# Revit family: IS_Connect_E5042_BIM_DE
name_source: partatom
category: Plumbing Fixtures
revit_build: Autodesk Revit MEP 2016 (Build: 20161004_0715(x64)
units: mm (PartAtom-declared; Revit-internal decimal feet)

## family parameters
Cut with Voids When Loaded = Yes
Host = Face
OmniClass Number = 23.45.05.14.14
OmniClass Title = Sinks/Lavatories
Part Type = Normal
Room Calculation Point = No
Round Connector Dimension = Use Diameter
Shared = Yes

## types (2) — shared parameters
Accessories = www.idealstandard.de\ersatzteile
AreaUnits = millimeters
Assembly Code = C1030200
AssetType = Fixed
BIMobject category = Basins
BarCode = 5017830446798
Brand url = http://www.idealstandard.co.uk
CodePerformance = DIN EN 14688 CL 15, DIN EN 31
Color = White
ConnectionType = Plumbing
CurrencyUnit = €
Date of publishing = 4/3/2017
Default Elevation = 850 mm  [stored 2.78871 ft]
Description = CONNECT countertop washbasin 480x480mm, 1 taphole, with overflow
DurationUnit = year
EAN code = https://5017830446798
Edition number = 1
ExpectedLife = 25
Features = CONNECT countertop washbasin 480x480mm, 1 taphole, with overflow
Finish = White
GrossWeight = 10,59 kg
IFC Classification = Sanitary Terminal
Installation instructions = http://www.idealstandard.de
InstallationDate = 1900-12-31T23:59:59
InstallationInstructions = www.idealstandard.de\produkte
LinearUnits = millimeters
Manufacturer name = Ideal Standard
ManufacturerURL = www.idealstandard.de
Material = Vitreous china
Material main = Ceramics
ModelNumber = E504201
ModelReference = IS Einbauwaschtisch CONNECT, rund, 1Hl., m.Ül., 480x480x175mm, Weiß
NBS Reference Code = 31-79
NBS Reference Description = Sinks, Wash Basins And Troughs
Nominal height = 175 mm  [stored 0.574147 ft]
Nominal width = 480 mm  [stored 1.5748 ft]
NominalLength = 480 mm  [stored 1.5748 ft]
OmniClass Code = 23-31 13 00
OmniClass Description = Sinks
Product Guid = 4080ecf9-aefb-4d4f-9e86-ad151e22f48a
Product SKU = E5042
Product data url = https://bimobject.com
Product family = CONNECT
Product group = Basin
Product url = http://www.idealstandard.de
ProductInformation = www.idealstandard.de
QR code = http://bimobject.com
Shape = Sculptured
Size = 480 x 480 x 175 mm
Space = Internal
Technical description = http://www.idealstandard.de
URL = www.idealstandard.de
Uniclass 1.4 Code = L7212
Uniclass 1.4 Description = Washbasins
Uniclass 2.0 Code = PR-31-79
Uniclass 2.0 Description = Sinks, Wash Basins And Troughs
Uniclass 2015 Code = Pr_40_20_96
Uniclass 2015 Name = Wash basins, sinks and troughs
Uniclass2015Code = Pr_40_20_96_18
Uniclass2015Title = Counter top wash basins
Uniclass2015Version = Products v1.1
Version = 1
VolumeUnits = Litres
WasteCover = ISI_IdealStandard_BasinMaterial_White3_Render
Weight Net (Kg) = 7.94
zero-valued in all types: CWFU, Cost, HWFU, NominalDepth, WFU

## per-type parameters (varying)
| type | BIMObjectName | Model | Name |
| E504201 CONNECT countertop washbasin 480x480mm, 1 taphole, with overflow | ISI_IdealStandard_Sinks_CONNECT_E504201 | E504201 | ISI_IdealStandard_Sinks_CONNECT_E504201 |
| E5042MA CONNECT countertop washbasin 480x480mm, 1 taphole, with overflow with Ideal Plus | ISI_IdealStandard_Sinks_CONNECT_E5042MA | E5042MA | ISI_IdealStandard_Sinks_CONNECT_E5042MA |

note: [stored X ft] marks values corroborated as IEEE doubles in the binary element streams (Revit-internal decimal feet)

## geometry (parser evidence)
native form markers: Blend x2, Sweep x3
no freeform markers — native parametric forms only
